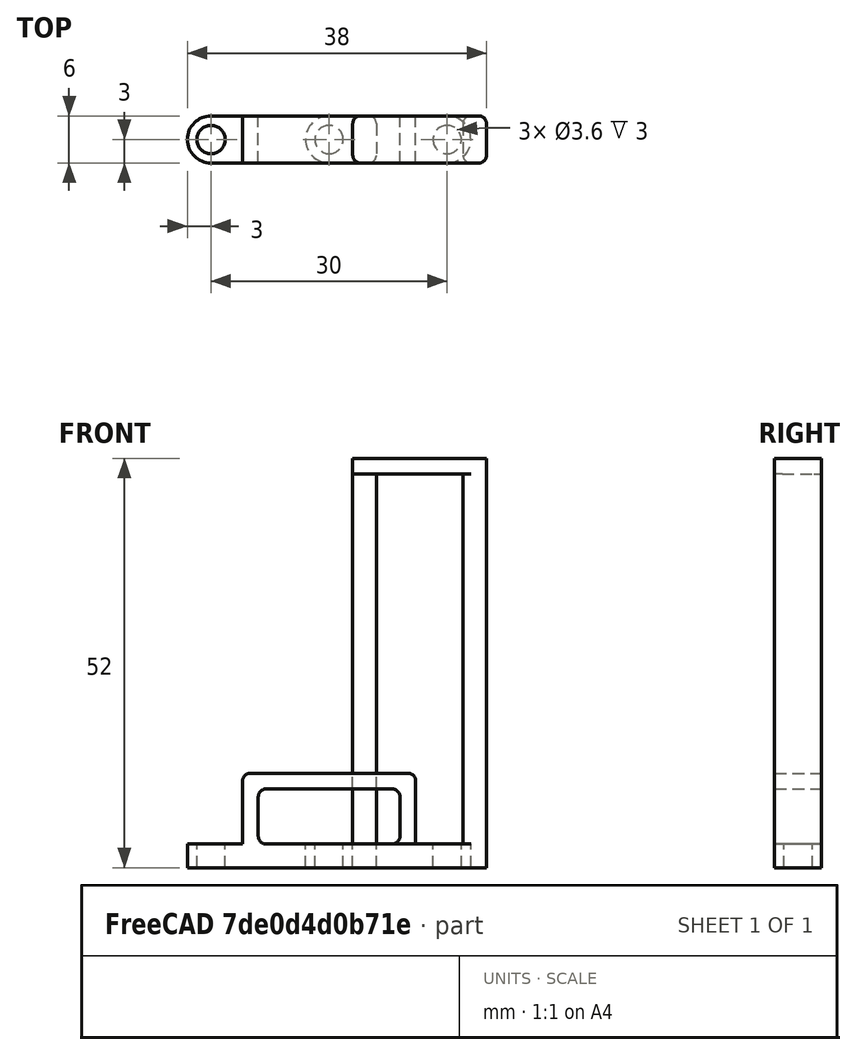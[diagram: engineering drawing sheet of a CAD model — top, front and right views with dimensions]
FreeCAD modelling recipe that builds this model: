
FCSTD DOCUMENT  (FreeCAD 0.19R23578 (Git))
Label: nema_wire_holder
License: All rights reserved
LicenseURL: http://en.wikipedia.org/wiki/All_rights_reserved
objects: Part::Box×6, Part::Fillet×5, Part::Cylinder×4, Part::MultiFuse×3, Part::Mirroring×2, Part::Cut×2, Part::FeaturePython×1
note: 22 computed .brp shape members not serialized (recipe doc carries the construction recipe); baked Part::Feature solids carry a one-line shape summary decoded from their .brp

FEATURE [Part::Cylinder] Cylinder  label="end cylinder"
  Angle = 360
  AttacherType = Attacher::AttachEngine3D
  Height = 3
  Placement = pos=(-15,0,0) rot=(0,0,1;0rad)
  Radius = 3
  expr: .Placement.Base.x = -<<bottom cube>>.Length / 2
  expr: Radius = <<central hole cube>>.Width / 2
  expr: Height = <<bottom cube>>.Height
FEATURE [Part::Box] Box  label="bottom cube"
  AttacherType = Attacher::AttachEngine3D
  Height = 3
  Length = 30
  Placement = pos=(-15,-3,0) rot=(0,0,1;0rad)
  Width = 6
  expr: Length = round((<<top cube>>.Length + Width) / 10) * 10
  expr: Width = <<central hole cube>>.Width
  expr: Height = <<central hole cube>>.Placement.Base.z
  expr: .Placement.Base.x = -Length / 2
  expr: .Placement.Base.y = -Width / 2
FEATURE [Part::Mirroring] Part__Mirroring  label="other end cylinder (Mirror #1)"
  Base = (0,0,0)
  Normal = (1,0,0)
  Source = -> Cylinder
FEATURE [Part::Box] Box001  label="top cube"
  AttacherType = Attacher::AttachEngine3D
  Height = 9
  Length = 22
  Placement = pos=(-11,-3,3) rot=(0,0,1;0rad)
  Width = 6
  expr: Height = <<central hole cube>>.Height + 2mm
  expr: .Placement.Base.z = <<central hole cube>>.Placement.Base.z
  expr: .Placement.Base.x = -Length / 2
  expr: Length = <<central hole cube>>.Length + 4mm
  expr: Width = <<central hole cube>>.Width
  expr: .Placement.Base.y = -Width / 2
FEATURE [Part::Box] Box002  label="central hole cube"
  AttacherType = Attacher::AttachEngine3D
  Height = 7
  Length = 18
  Placement = pos=(-9,-3,3) rot=(0,0,1;0rad)
  Width = 6
  expr: .Placement.Base.y = -Width / 2
  expr: .Placement.Base.x = -Length / 2
FEATURE [Part::Fillet] Fillet  label="central hole fillet"
  Base = -> Box002
  Edges = 4 edges r=1: [Edge2,Edge4,Edge6,Edge8]
FEATURE [Part::Fillet] Fillet001  label="top cube fillet"
  Base = -> Box001
  Edges = 2 edges r=1: [Edge2,Edge6]
FEATURE [Part::MultiFuse] Fusion  label="body fusion"
  Shapes = -> [Cylinder,Part__Mirroring,Box,Fillet001]
FEATURE [Part::Cylinder] Cylinder001  label="bolt hole"
  Angle = 360
  AttacherType = Attacher::AttachEngine3D
  Height = 10
  Placement = pos=(-15,0,0) rot=(0,0,1;0rad)
  Radius = 1.8
  expr: .Placement.Base.x = -<<bottom cube>>.Length / 2
FEATURE [Part::Mirroring] Part__Mirroring001  label="bolt hole (Mirror #2)"
  Base = (0,0,0)
  Normal = (1,0,0)
  Source = -> Cylinder001
FEATURE [Part::MultiFuse] Fusion001  label="extract fusion"
  Shapes = -> [Part__Mirroring001,Cylinder001,Fillet]
FEATURE [Part::Cut] Cut  label="wire holder"
  Base = -> Fusion
  Tool = -> Fusion001
FEATURE [Part::Cylinder] Cylinder002  label="bolt hole001"
  Angle = 360
  AttacherType = Attacher::AttachEngine3D
  Height = 10
  Radius = 1.8
FEATURE [Part::Cylinder] Cylinder003  label="hole base cylinder"
  Angle = 360
  AttacherType = Attacher::AttachEngine3D
  Height = 3
  Radius = 3
FEATURE [Part::Box] Box003  label="bottom cube001"
  AttacherType = Attacher::AttachEngine3D
  Height = 3
  Length = 20
  Placement = pos=(0,-3,0) rot=(0,0,1;0rad)
  Width = 6
  expr: Height = <<hole base cylinder>>.Height
  expr: Width = <<hole base cylinder>>.Radius * 2
  expr: .Placement.Base.y = -Width / 2
FEATURE [Part::Box] Box005  label="vert cube001"
  AttacherType = Attacher::AttachEngine3D
  Height = 50
  Length = 3
  Placement = pos=(3,-3,0) rot=(0,0,1;0rad)
  Width = 6
  expr: .Placement.Base.x = <<hole base cylinder>>.Radius
  expr: .Placement.Base.y = -Width / 2
  expr: Width = <<bottom cube001>>.Width
FEATURE [Part::Fillet] Fillet002  label="vert cube fillet"
  Base = -> Box005
  Edges = 4 edges r=1: [Edge1,Edge3,Edge5,Edge7]
FEATURE [Part::FeaturePython] Array  label="vert cube array"  # Draft array (typed FeaturePython)
  Angle = 360
  ArrayType = 0
  Axis = (0,0,1)
  Base = -> Fillet002
  Center = (0,0,0)
  Count = 2
  ExpandArray = false
  Fuse = false
  IntervalAxis = (0,0,0)
  IntervalX = (14,0,0)
  IntervalY = (0,100,0)
  IntervalZ = (0,0,100)
  NumberCircles = 3
  NumberPolar = 5
  NumberX = 2
  NumberY = 1
  NumberZ = 1
  PlacementList = 2 placements: [(0,0,0),(14,0,0)]
  RadialDistance = 50
  ScaleList = (2) [(1,1,1),(1,1,1)]
  Symmetry = 1
  TangentialDistance = 25
  expr: .IntervalX.x = <<bottom cube001>>.Length - <<hole base cylinder>>.Radius - <<vert cube001>>.Length
FEATURE [Part::Fillet] Fillet003  label="bottom cube fillet"
  Base = -> Box003
  Edges = 2 edges r=1: [Edge5,Edge7]
FEATURE [Part::Box] Box006  label="top cube001"
  AttacherType = Attacher::AttachEngine3D
  Height = 2
  Length = 17
  Placement = pos=(3,-3,50) rot=(0,0,1;0rad)
  Width = 6
  expr: Width = <<bottom cube001>>.Width
  expr: .Placement.Base.y = -Width / 2
  expr: .Placement.Base.x = <<vert cube001>>.Placement.Base.x
  expr: Length = <<vert cube array>>.IntervalX.x + <<vert cube001>>.Length
  expr: .Placement.Base.z = <<vert cube001>>.Height
FEATURE [Part::Fillet] Fillet004
  Base = -> Box006
  Edges = 4 edges r=1: [Edge1,Edge3,Edge5,Edge7]
FEATURE [Part::MultiFuse] Fusion002  label="high wire holder fusion"
  Shapes = -> [Cylinder003,Array,Fillet003,Fillet004]
FEATURE [Part::Cut] Cut001  label="high wire holder cut"
  Base = -> Fusion002
  Tool = -> Cylinder002
